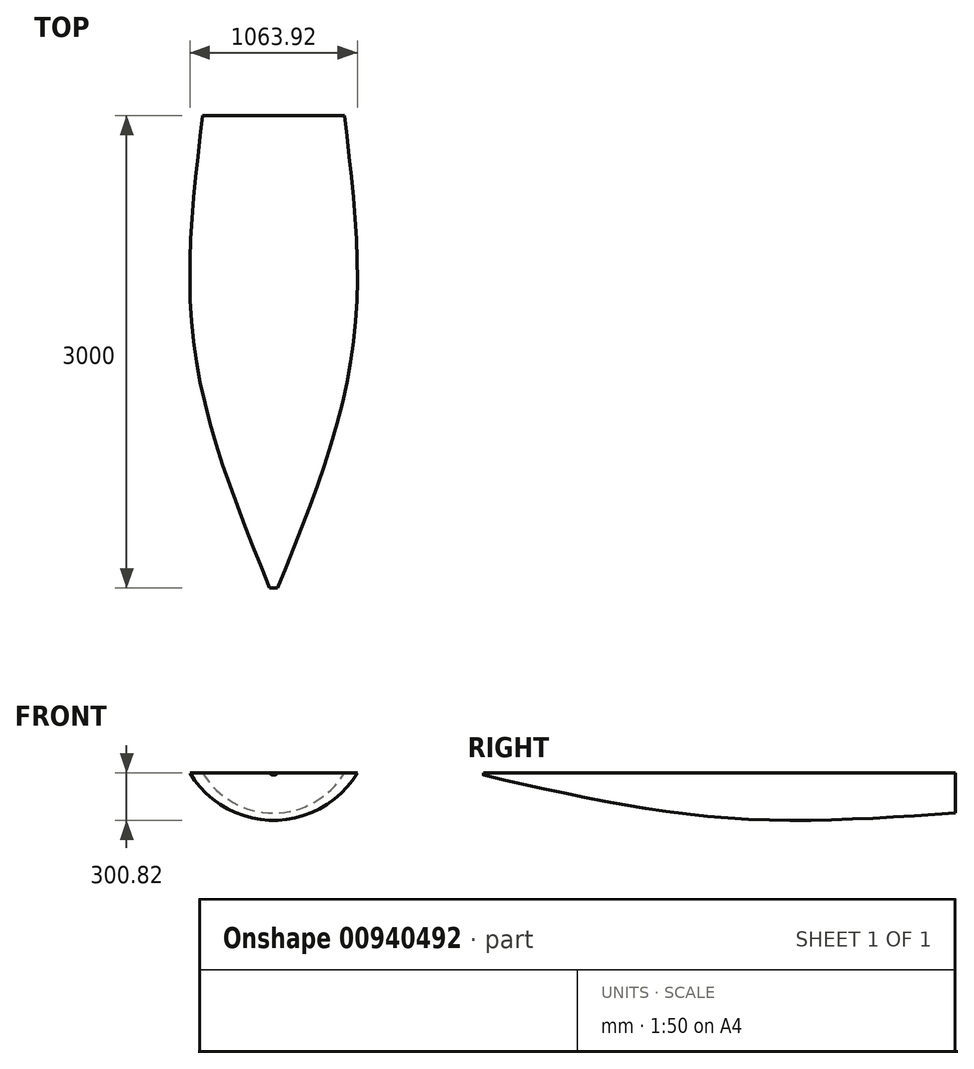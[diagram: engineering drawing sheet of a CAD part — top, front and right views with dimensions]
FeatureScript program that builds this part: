
annotation { "Feature Type Name" : "Feature", "Feature Type Description" : "" }
export const myFeature = defineFeature(function(context is Context, id is Id, definition is map)
    precondition{}
    {
        {
            var Q0;
            Q0=qCreatedBy(makeId("Front.planeOp"),FACE);
            var sketch = newSketch(context, id + "F0", { "sketchPlane" : qUnion([Q0])});
            skLineSegment(sketch, "E0", {"start": v(0, 0) * mm, "end": v(-500, 0) * mm});
            skLineSegment(sketch, "E1", {"start": v(0, 0) * mm, "end": v(500, 0) * mm});
            skArc(sketch, "E2", {"start": v(-500, 0) * mm, "mid": v(0, -282.54) * mm, "end": v(500, 0) * mm});
            skSolve(sketch);
        }
        {
            var Q0;
            Q0=qCreatedBy(makeId("Front.planeOp"),FACE);
            cPlane(context, id + "F1", {"entities" : qUnion([Q0]), "cplaneType" : CPlaneType.OFFSET, "offset" : 1500 * mm, "oppositeDirection" : true, "width" : 150 * mm, "height" : 150 * mm});
        }
        {
            var Q0;
            Q0=qCreatedBy(id+"F1.planeOp",FACE);
            var sketch = newSketch(context, id + "F2", { "sketchPlane" : qUnion([Q0])});
            skLineSegment(sketch, "E3", {"start": v(0, 0) * mm, "end": v(-450, 0) * mm});
            skLineSegment(sketch, "E4", {"start": v(0, 0) * mm, "end": v(450, 0) * mm});
            skArc(sketch, "E5", {"start": v(-450, 0) * mm, "mid": v(0, -255.2) * mm, "end": v(450, 0) * mm});
            skSolve(sketch);
        }
        {
            var Q0;
            Q0=qCreatedBy(makeId("Front.planeOp"),FACE);
            cPlane(context, id + "F3", {"entities" : qUnion([Q0]), "cplaneType" : CPlaneType.OFFSET, "offset" : 1000 * mm, "width" : 150 * mm, "height" : 150 * mm});
        }
        {
            var Q0;
            Q0=qCreatedBy(id+"F3.planeOp",FACE);
            cPlane(context, id + "F4", {"entities" : qUnion([Q0]), "cplaneType" : CPlaneType.OFFSET, "offset" : 500 * mm, "width" : 150 * mm, "height" : 150 * mm});
        }
        {
            var Q0;
            Q0=qCreatedBy(id+"F4.planeOp",FACE);
            var sketch = newSketch(context, id + "F5", { "sketchPlane" : qUnion([Q0])});
            skLineSegment(sketch, "E6", {"start": v(0, 0) * mm, "end": v(-25, 0) * mm});
            skLineSegment(sketch, "E7", {"start": v(0, 0) * mm, "end": v(25, 0) * mm});
            skArc(sketch, "E8", {"start": v(-25, 0) * mm, "mid": v(0, -14.08) * mm, "end": v(25, 0) * mm});
            skSolve(sketch);
        }
        {
            var Q0;
            Q0=makeQuery(id+"F5.imprint","IMPRINT",FACE,{"disambiguationData":[TD([[makeQuery(id+"F5.imprint","IMPRINT",EDGE,{"derivedFrom":sQuery(id+"F5.wireOp",EDGE,"E6")}),1.0]])]});
            var Q1;
            Q1=makeQuery(id+"F0.imprint","IMPRINT",FACE,{"disambiguationData":[TD([[makeQuery(id+"F0.imprint","IMPRINT",EDGE,{"derivedFrom":sQuery(id+"F0.wireOp",EDGE,"E0")}),1.0]])]});
            var Q2;
            Q2=makeQuery(id+"F2.imprint","IMPRINT",FACE,{"disambiguationData":[TD([[makeQuery(id+"F2.imprint","IMPRINT",EDGE,{"derivedFrom":sQuery(id+"F2.wireOp",EDGE,"E3")}),1.0]])]});
            loft(context, id + "F6", {"sheetProfilesArray" : [{ "sheetProfileEntities" : qUnion([Q0]) }, { "sheetProfileEntities" : qUnion([Q1]) }, { "sheetProfileEntities" : qUnion([Q2]) }]});
        }
    });
